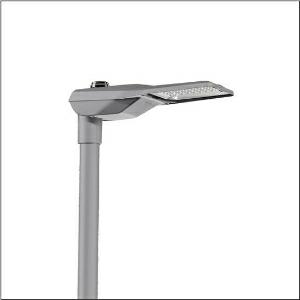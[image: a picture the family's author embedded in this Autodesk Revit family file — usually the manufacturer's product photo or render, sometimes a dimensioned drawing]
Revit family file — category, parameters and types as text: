
# Revit family: streetlight_sl_21_mini___p1_0a_5xe6a37n08gb_7347
name_source: partatom
category: Lighting Fixtures
units: mm (PartAtom-declared; Revit-internal decimal feet)

## family parameters
Cut with Voids When Loaded = No
Host = Face
Light Source = No
Part Type = Normal
Room Calculation Point = No
Round Connector Dimension = Use Diameter
Shared = No

## types (1)
- --- (1 x LED, 5940 lm, 40.4 W, 3000K)
    Apparent Load = 40 VA
    CIE Flux Codes = 21 50 90 100 100
    Color Rendering = 70
    Color Temperature = 3000K
    Default Elevation = 1800 mm
    Description = Streetlight SL 21 mini, mast luminaire, primary light control with lens, of PMMA, primary optical cover: cover, of toughened safety glass, transparent, light distribution: P1.0a, light emission: direct distribution, primary light characteristic: asymmetric, installation type: side-entry, LED, 3G 1.5mm², High Power LED, rated luminous flux: 5.940lm, luminous efficacy: 147lm/W, light colour: 730, colour temperature: 3000K, control gear: NEMA (7pin), control: overheat protection, pre-setting: linear dimming characteristic, constant luminous flux control, time-dependent luminous flux control, flexible luminous flux parameterisation, mains connection: 230..240V, AC, 50/60Hz, connection cable pre-assembled, cable length: 8,5m, wiring characteristics: H07RN-F, start of lifetime: 40W, end of service life: 41W, reduction: 19W, luminaire housing, of diecast aluminium (EN AC-44300), powder-coated, Siteco® metallic grey (DB 702S), corrosivity category C5 mid according to DIN EN ISO 12944, multi-level sealing system, sealing non-destructively replaceable, inclination adjustable: 0°, 5°, 10°, 15°, length: 628mm, width: 235mm, height: 110mm, spigot size: 42mm (side-entry), mounting height: 4..8m, protection rating (complete): IP66, insulation class (complete): insulation class I (protective earthing), certification: CE, ENEC, ENEC+, VDE, impact resistance: IK09, permissible operating ambient temperature for outdoor applications: -40..+50°C, standard-compliant lighting for roads and squares, packaging unit: 1 piece

Light Distribution: P1.0a
    Height = 110 mm
    Lamp = 1 x LED
    Lamp Light Flux = 5940 lm
    Lamp Power = 40.4 W
    Lamp count = 1
    Length = 625 mm
    Luminous efficacy = 147 lm/W
    Manufacturer = Siteco
    ModVariant = No
    Model = 5XE6A37N08GB
    Number of Poles = 1
    OnlyDefault = Yes
    Power Factor = 1
    Product Name = Streetlight SL 21 mini | P1.0a
    Product group = mast luminaire | pylon top
    ProductGroupID = 6100
    Protection Class = Protection class I
    Protection Degree = IP 66
    RLX_Detail_Level = 1
    RLX_Emergency_Light_Flux = 0 lm
    RLX_Emergency_Type = 0
    RLX_Emergency_Type_DB = No
    RlxData = <blob elided: 103177 chars, md5=253b5e38>
    Socket = socket
    Standby Power = 0 W
    System Light Flux = 5940 lm
    System Power = 40 W
    Type Comments = factory setting: luminous flux: 100 % | dim-lin: 254 | 812 mA
    Type Image = l_1294379.jpg
    URL = http://relux.com
    VarID = @adj_132148
    Voltage = 0 V
    Weight = 0.00 kg
    Width = 234 mm

## geometry (parser evidence)
native form markers: Blend x4, Sweep x11
no freeform markers — native parametric forms only
